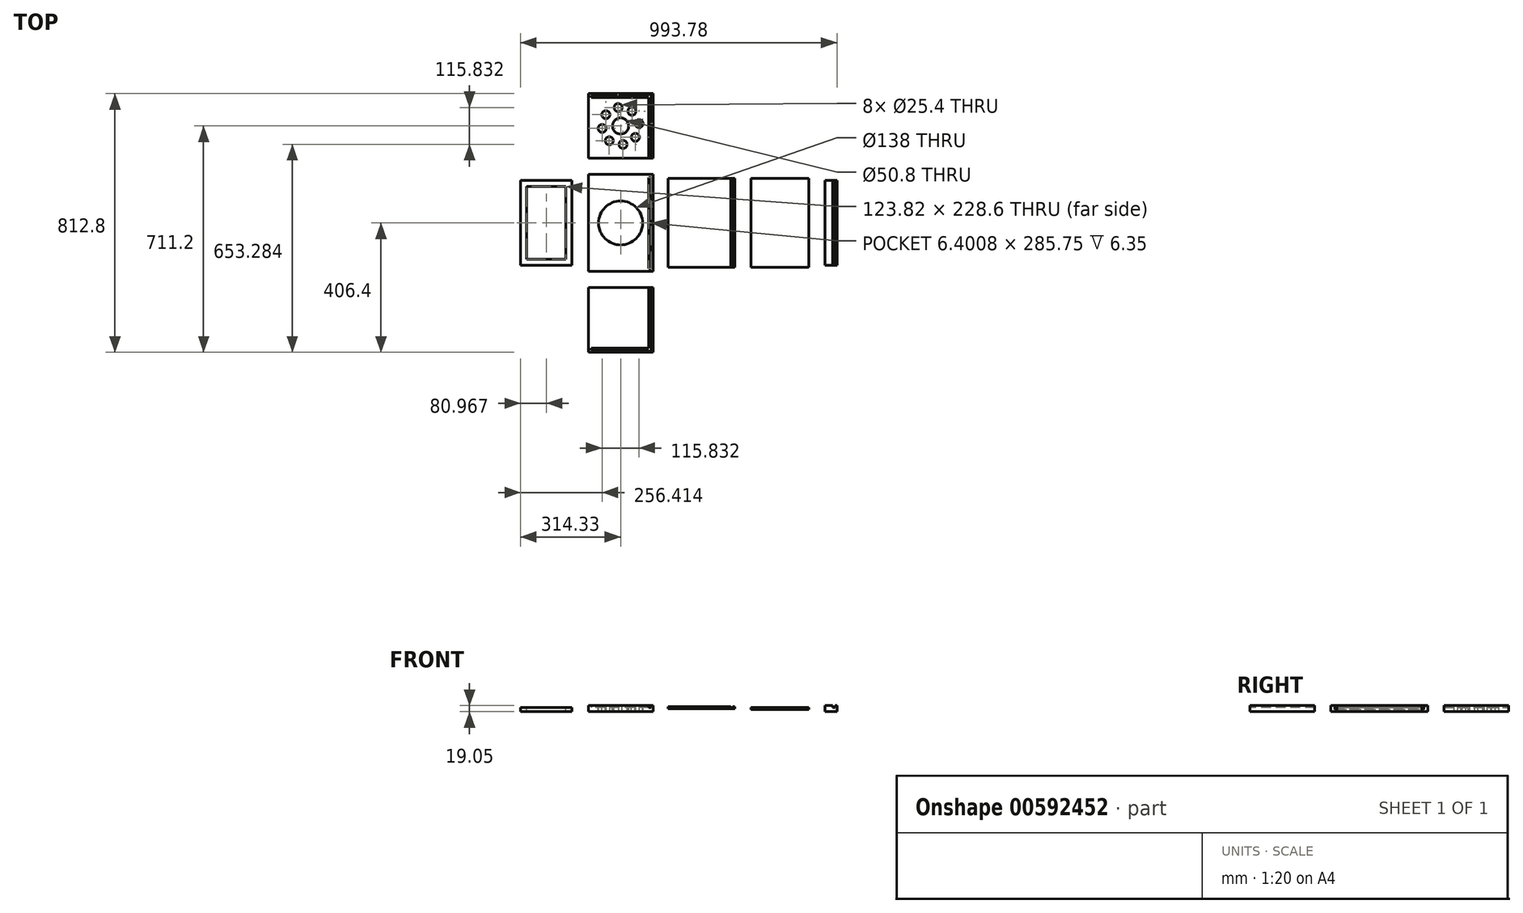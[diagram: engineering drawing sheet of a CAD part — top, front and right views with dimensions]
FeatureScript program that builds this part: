
annotation { "Feature Type Name" : "Feature", "Feature Type Description" : "" }
export const myFeature = defineFeature(function(context is Context, id is Id, definition is map)
    precondition{}
    {
        {
            var Q0;
            Q0=qCreatedBy(makeId("Top.planeOp"),FACE);
            var sketch = newSketch(context, id + "F0", { "sketchPlane" : qUnion([Q0])});
            skLineSegment(sketch, "E0.bottom", {"start": v(101.6, -152.4) * mm, "end": v(-101.6, -152.4) * mm});
            skLineSegment(sketch, "E0.top", {"start": v(101.6, 152.4) * mm, "end": v(-101.6, 152.4) * mm});
            skLineSegment(sketch, "E0.left", {"start": v(101.6, -152.4) * mm, "end": v(101.6, 152.4) * mm});
            skLineSegment(sketch, "E0.right", {"start": v(-101.6, -152.4) * mm, "end": v(-101.6, 152.4) * mm});
            skPoint(sketch, "E0.middle", {"position": v(0, 0) * mm});
            skCircle(sketch, "E1", {"center": v(0, 0) * mm, "radius": 69 * mm});
            skLineSegment(sketch, "E2.bottom", {"start": v(88.85, 142.88) * mm, "end": v(95.25, 142.88) * mm});
            skLineSegment(sketch, "E2.top", {"start": v(88.85, -142.88) * mm, "end": v(95.25, -142.88) * mm});
            skLineSegment(sketch, "E2.left", {"start": v(88.85, 142.88) * mm, "end": v(88.85, -142.88) * mm});
            skLineSegment(sketch, "E2.right", {"start": v(95.25, 142.88) * mm, "end": v(95.25, -142.88) * mm});
            skSolve(sketch);
        }
        {
            var Q0;
            Q0=makeQuery(id+"F0.imprint","IMPRINT",FACE,{"disambiguationData":[TD([[makeQuery(id+"F0.imprint","IMPRINT",EDGE,{"derivedFrom":sQuery(id+"F0.wireOp",EDGE,"E0.bottom")}),-1.0]])]});
            var Q1;
            {var subQ0=sQuery(id+"F0.wireOp",EDGE,"E0.right");Q1=makeQuery(id+"F0.imprint","IMPRINT",FACE,{"disambiguationData":[TD([[makeQuery(id+"F0.imprint","IMPRINT",EDGE,{"derivedFrom":subQ0}),-1.0]])]});}
            var Q2;
            Q2=makeQuery(id+"F0.imprint","IMPRINT",FACE,{"disambiguationData":[TD([[makeQuery(id+"F0.imprint","IMPRINT",EDGE,{"derivedFrom":sQuery(id+"F0.wireOp",EDGE,"E2.bottom")}),-1.0]])]});
            extrude(context, id + "F1", {"entities" : qUnion([Q0, Q1, Q2]), "oppositeDirection" : true, "depth" : 12.7 * mm, "offsetDistance" : 25.4 * mm});
        }
        {
            var Q0;
            {var subQ0=sQuery(id+"F0.wireOp",EDGE,"E0.right");Q0=makeQuery(id+"F0.imprint","IMPRINT",FACE,{"disambiguationData":[TD([[makeQuery(id+"F0.imprint","IMPRINT",EDGE,{"derivedFrom":subQ0}),-1.0]])]});}
            var Q1;
            {var subQ0=sQuery(id+"F0.wireOp",EDGE,"E0.left");Q1=makeQuery(id+"F0.imprint","IMPRINT",FACE,{"disambiguationData":[TD([[makeQuery(id+"F0.imprint","IMPRINT",EDGE,{"derivedFrom":subQ0}),1.0]])]});}
            extrude(context, id + "F2", {"entities" : qUnion([Q0, Q1]), "operationType" : NewBodyOperationType.ADD, "depth" : 6.35 * mm, "offsetDistance" : 25.4 * mm});
        }
        {
            var Q0;
            Q0=qCreatedBy(makeId("Top.planeOp"),FACE);
            var sketch = newSketch(context, id + "F3", { "sketchPlane" : qUnion([Q0])});
            skLineSegment(sketch, "E3.bottom", {"start": v(101.6, -406.4) * mm, "end": v(-101.6, -406.4) * mm});
            skLineSegment(sketch, "E3.top", {"start": v(101.6, -203.2) * mm, "end": v(-101.6, -203.2) * mm});
            skLineSegment(sketch, "E3.left", {"start": v(101.6, -406.4) * mm, "end": v(101.6, -203.2) * mm});
            skLineSegment(sketch, "E3.right", {"start": v(-101.6, -406.4) * mm, "end": v(-101.6, -203.2) * mm});
            skPoint(sketch, "E3.middle", {"position": v(0, -304.8) * mm});
            skPoint(sketch, "E4.0", {"position": v(101.6, -152.4) * mm});
            skPoint(sketch, "E4.1", {"position": v(-101.6, -152.4) * mm});
            skPoint(sketch, "E5.0", {"position": v(88.85, -142.88) * mm});
            skPoint(sketch, "E5.1", {"position": v(95.25, -142.88) * mm});
            skLineSegment(sketch, "E6.bottom", {"start": v(88.85, -200.03) * mm, "end": v(95.25, -200.03) * mm});
            skLineSegment(sketch, "E6.top", {"start": v(88.85, -409.58) * mm, "end": v(95.25, -409.58) * mm});
            skLineSegment(sketch, "E6.left", {"start": v(88.85, -200.03) * mm, "end": v(88.85, -409.58) * mm});
            skLineSegment(sketch, "E6.right", {"start": v(95.25, -200.03) * mm, "end": v(95.25, -409.58) * mm});
            skLineSegment(sketch, "E7.bottom", {"start": v(91.54, -393.65) * mm, "end": v(-92.07, -393.65) * mm});
            skLineSegment(sketch, "E7.top", {"start": v(91.54, -400.05) * mm, "end": v(-92.07, -400.05) * mm});
            skLineSegment(sketch, "E7.left", {"start": v(91.54, -393.65) * mm, "end": v(91.54, -400.05) * mm});
            skLineSegment(sketch, "E7.right", {"start": v(-92.07, -393.65) * mm, "end": v(-92.07, -400.05) * mm});
            skSolve(sketch);
        }
        {
            var Q0;
            Q0=makeQuery(id+"F3.imprint","IMPRINT",FACE,{"disambiguationData":[TD([[makeQuery(id+"F3.imprint","IMPRINT",EDGE,{"derivedFrom":sQuery(id+"F3.wireOp",EDGE,"E3.bottom")}),-1.0]])]});
            var Q1;
            {var subQ5=sQuery(id+"F3.wireOp",EDGE,"E3.right");Q1=makeQuery(id+"F3.imprint","IMPRINT",FACE,{"disambiguationData":[TD([[makeQuery(id+"F3.imprint","IMPRINT",EDGE,{"derivedFrom":subQ5}),-1.0]])]});}
            var Q2;
            {var subQ11=sQuery(id+"F3.wireOp",EDGE,"E7.left");Q2=makeQuery(id+"F3.imprint","IMPRINT",FACE,{"disambiguationData":[TD([[makeQuery(id+"F3.imprint","IMPRINT",EDGE,{"derivedFrom":subQ11}),1.0]])]});}
            var Q3;
            {var subQ5=sQuery(id+"F3.wireOp",EDGE,"E7.right");Q3=makeQuery(id+"F3.imprint","IMPRINT",FACE,{"disambiguationData":[TD([[makeQuery(id+"F3.imprint","IMPRINT",EDGE,{"derivedFrom":subQ5}),1.0]])]});}
            var Q4;
            {var subQ5=sQuery(id+"F3.wireOp",EDGE,"E7.left");Q4=makeQuery(id+"F3.imprint","IMPRINT",FACE,{"disambiguationData":[TD([[makeQuery(id+"F3.imprint","IMPRINT",EDGE,{"derivedFrom":subQ5}),-1.0]])]});}
            extrude(context, id + "F4", {"entities" : qUnion([Q0, Q1, Q2, Q3, Q4]), "oppositeDirection" : true, "depth" : 12.7 * mm, "offsetDistance" : 25.4 * mm});
        }
        {
            var Q0;
            {var subQ0=sQuery(id+"F3.wireOp",EDGE,"E3.right");Q0=makeQuery(id+"F3.imprint","IMPRINT",FACE,{"disambiguationData":[TD([[makeQuery(id+"F3.imprint","IMPRINT",EDGE,{"derivedFrom":subQ0}),-1.0]])]});}
            var Q1;
            {var subQ0=sQuery(id+"F3.wireOp",EDGE,"E3.left");Q1=makeQuery(id+"F3.imprint","IMPRINT",FACE,{"disambiguationData":[TD([[makeQuery(id+"F3.imprint","IMPRINT",EDGE,{"derivedFrom":subQ0}),1.0]])]});}
            extrude(context, id + "F5", {"entities" : qUnion([Q0, Q1]), "operationType" : NewBodyOperationType.ADD, "depth" : 6.35 * mm, "offsetDistance" : 25.4 * mm});
        }
        {
            var Q0;
            Q0=qCreatedBy(makeId("Top.planeOp"),FACE);
            var sketch = newSketch(context, id + "F6", { "sketchPlane" : qUnion([Q0])});
            skLineSegment(sketch, "E8.bottom", {"start": v(101.6, 203.2) * mm, "end": v(-101.6, 203.2) * mm});
            skLineSegment(sketch, "E8.top", {"start": v(101.6, 406.4) * mm, "end": v(-101.6, 406.4) * mm});
            skLineSegment(sketch, "E8.left", {"start": v(101.6, 203.2) * mm, "end": v(101.6, 406.4) * mm});
            skLineSegment(sketch, "E8.right", {"start": v(-101.6, 203.2) * mm, "end": v(-101.6, 406.4) * mm});
            skPoint(sketch, "E9.0", {"position": v(88.85, 142.88) * mm});
            skPoint(sketch, "E9.1", {"position": v(95.25, 142.88) * mm});
            skLineSegment(sketch, "E10.bottom", {"start": v(88.85, 200.03) * mm, "end": v(95.25, 200.03) * mm});
            skLineSegment(sketch, "E10.top", {"start": v(88.85, 409.58) * mm, "end": v(95.25, 409.58) * mm});
            skLineSegment(sketch, "E10.left", {"start": v(88.85, 200.03) * mm, "end": v(88.85, 409.58) * mm});
            skLineSegment(sketch, "E10.right", {"start": v(95.25, 200.03) * mm, "end": v(95.25, 409.58) * mm});
            skLineSegment(sketch, "E11.bottom", {"start": v(91.88, 400.05) * mm, "end": v(-92.08, 400.05) * mm});
            skLineSegment(sketch, "E11.top", {"start": v(91.88, 393.65) * mm, "end": v(-92.08, 393.65) * mm});
            skLineSegment(sketch, "E11.left", {"start": v(91.88, 400.05) * mm, "end": v(91.88, 393.65) * mm});
            skLineSegment(sketch, "E11.right", {"start": v(-92.08, 400.05) * mm, "end": v(-92.08, 393.65) * mm});
            skCircle(sketch, "E12", {"center": v(-46.37, 340.34) * mm, "radius": 12.7 * mm});
            skCircle(sketch, "E13.1.0", {"center": v(-57.92, 297.14) * mm, "radius": 12.7 * mm});
            skCircle(sketch, "E13.2.0", {"center": v(-35.54, 258.43) * mm, "radius": 12.7 * mm});
            skCircle(sketch, "E13.3.0", {"center": v(7.66, 246.88) * mm, "radius": 12.7 * mm});
            skCircle(sketch, "E13.4.0", {"center": v(46.37, 269.26) * mm, "radius": 12.7 * mm});
            skCircle(sketch, "E13.5.0", {"center": v(57.92, 312.46) * mm, "radius": 12.7 * mm});
            skCircle(sketch, "E13.6.0", {"center": v(35.54, 351.17) * mm, "radius": 12.7 * mm});
            skCircle(sketch, "E13.7.0", {"center": v(-7.66, 362.72) * mm, "radius": 12.7 * mm});
            skPoint(sketch, "E13.center", {"position": v(0, 304.8) * mm});
            skCircle(sketch, "E14", {"center": v(0, 304.8) * mm, "radius": 25.4 * mm});
            skSolve(sketch);
        }
        {
            var Q0;
            Q0=makeQuery(id+"F6.imprint","IMPRINT",FACE,{"disambiguationData":[TD([[makeQuery(id+"F6.imprint","IMPRINT",EDGE,{"derivedFrom":sQuery(id+"F6.wireOp",EDGE,"E8.bottom")}),-1.0]])]});
            var Q1;
            {var subQ5=sQuery(id+"F6.wireOp",EDGE,"E11.right");Q1=makeQuery(id+"F6.imprint","IMPRINT",FACE,{"disambiguationData":[TD([[makeQuery(id+"F6.imprint","IMPRINT",EDGE,{"derivedFrom":subQ5}),1.0]])]});}
            var Q2;
            {var subQ5=sQuery(id+"F6.wireOp",EDGE,"E8.right");Q2=makeQuery(id+"F6.imprint","IMPRINT",FACE,{"disambiguationData":[TD([[makeQuery(id+"F6.imprint","IMPRINT",EDGE,{"derivedFrom":subQ5}),-1.0]])]});}
            var Q3;
            {var subQ11=sQuery(id+"F6.wireOp",EDGE,"E11.left");Q3=makeQuery(id+"F6.imprint","IMPRINT",FACE,{"disambiguationData":[TD([[makeQuery(id+"F6.imprint","IMPRINT",EDGE,{"derivedFrom":subQ11}),1.0]])]});}
            var Q4;
            {var subQ5=sQuery(id+"F6.wireOp",EDGE,"E11.left");Q4=makeQuery(id+"F6.imprint","IMPRINT",FACE,{"disambiguationData":[TD([[makeQuery(id+"F6.imprint","IMPRINT",EDGE,{"derivedFrom":subQ5}),-1.0]])]});}
            extrude(context, id + "F7", {"entities" : qUnion([Q0, Q1, Q2, Q3, Q4]), "oppositeDirection" : true, "depth" : 12.7 * mm, "offsetDistance" : 25.4 * mm});
        }
        {
            var Q0;
            {var subQ0=sQuery(id+"F6.wireOp",EDGE,"E8.right");Q0=makeQuery(id+"F6.imprint","IMPRINT",FACE,{"disambiguationData":[TD([[makeQuery(id+"F6.imprint","IMPRINT",EDGE,{"derivedFrom":subQ0}),-1.0]])]});}
            var Q1;
            {var subQ0=sQuery(id+"F6.wireOp",EDGE,"E8.left");Q1=makeQuery(id+"F6.imprint","IMPRINT",FACE,{"disambiguationData":[TD([[makeQuery(id+"F6.imprint","IMPRINT",EDGE,{"derivedFrom":subQ0}),1.0]])]});}
            extrude(context, id + "F8", {"entities" : qUnion([Q0, Q1]), "operationType" : NewBodyOperationType.ADD, "depth" : 6.35 * mm, "offsetDistance" : 25.4 * mm});
        }
        {
            var Q0;
            Q0=qCreatedBy(makeId("Top.planeOp"),FACE);
            var sketch = newSketch(context, id + "F9", { "sketchPlane" : qUnion([Q0])});
            skLineSegment(sketch, "E15.bottom", {"start": v(358.8, -139.7) * mm, "end": v(149.25, -139.7) * mm});
            skLineSegment(sketch, "E15.top", {"start": v(358.8, 139.7) * mm, "end": v(149.25, 139.7) * mm});
            skLineSegment(sketch, "E15.left", {"start": v(358.8, -139.7) * mm, "end": v(358.8, 139.7) * mm});
            skLineSegment(sketch, "E15.right", {"start": v(149.25, -139.7) * mm, "end": v(149.25, 139.7) * mm});
            skPoint(sketch, "E15.middle", {"position": v(254.02, 0) * mm});
            skLineSegment(sketch, "E16.bottom", {"start": v(346.05, 142.88) * mm, "end": v(352.45, 142.88) * mm});
            skLineSegment(sketch, "E16.top", {"start": v(346.05, -142.88) * mm, "end": v(352.45, -142.88) * mm});
            skLineSegment(sketch, "E16.left", {"start": v(346.05, 142.88) * mm, "end": v(346.05, -142.88) * mm});
            skLineSegment(sketch, "E16.right", {"start": v(352.45, 142.88) * mm, "end": v(352.45, -142.88) * mm});
            skSolve(sketch);
        }
        {
            var Q0;
            {var subQ0=sQuery(id+"F9.wireOp",EDGE,"E15.left");Q0=makeQuery(id+"F9.imprint","IMPRINT",FACE,{"disambiguationData":[TD([[makeQuery(id+"F9.imprint","IMPRINT",EDGE,{"derivedFrom":subQ0}),1.0]])]});}
            var Q1;
            {var subQ0=sQuery(id+"F9.wireOp",EDGE,"E16.right");var subQ1=sQuery(id+"F9.wireOp",EDGE,"E15.bottom");var subQ2=makeQuery(id+"F9.imprint","INTERSECT",VERTEX,{"derivedFrom":[subQ1,subQ0]});Q1=makeQuery(id+"F9.imprint","IMPRINT",FACE,{"disambiguationData":[TD([[makeQuery(id+"F9.imprint","IMPRINT",EDGE,{"disambiguationData":[TD([[subQ2,-1.0]])],"derivedFrom":subQ1}),-1.0]])]});}
            var Q2;
            {var subQ0=sQuery(id+"F9.wireOp",EDGE,"E15.right");Q2=makeQuery(id+"F9.imprint","IMPRINT",FACE,{"disambiguationData":[TD([[makeQuery(id+"F9.imprint","IMPRINT",EDGE,{"derivedFrom":subQ0}),-1.0]])]});}
            extrude(context, id + "F10", {"entities" : qUnion([Q0, Q1, Q2]), "oppositeDirection" : true, "depth" : 3.2 * mm, "offsetDistance" : 25.4 * mm});
        }
        {
            var Q0;
            Q0=qCreatedBy(makeId("Top.planeOp"),FACE);
            var sketch = newSketch(context, id + "F11", { "sketchPlane" : qUnion([Q0])});
            skLineSegment(sketch, "E17.bottom", {"start": v(-152.4, -133.35) * mm, "end": v(-314.33, -133.35) * mm});
            skLineSegment(sketch, "E17.top", {"start": v(-152.4, 133.35) * mm, "end": v(-314.33, 133.35) * mm});
            skLineSegment(sketch, "E17.left", {"start": v(-152.4, -133.35) * mm, "end": v(-152.4, 133.35) * mm});
            skLineSegment(sketch, "E17.right", {"start": v(-314.33, -133.35) * mm, "end": v(-314.33, 133.35) * mm});
            skPoint(sketch, "E17.middle", {"position": v(-233.36, 0) * mm});
            skLineSegment(sketch, "E18.bottom", {"start": v(-171.45, -114.3) * mm, "end": v(-295.28, -114.3) * mm});
            skLineSegment(sketch, "E18.top", {"start": v(-171.45, 114.3) * mm, "end": v(-295.28, 114.3) * mm});
            skLineSegment(sketch, "E18.left", {"start": v(-171.45, -114.3) * mm, "end": v(-171.45, 114.3) * mm});
            skLineSegment(sketch, "E18.right", {"start": v(-295.28, -114.3) * mm, "end": v(-295.28, 114.3) * mm});
            skSolve(sketch);
        }
        {
            var Q0;
            Q0=makeQuery(id+"F11.imprint","IMPRINT",FACE,{"disambiguationData":[TD([[makeQuery(id+"F11.imprint","IMPRINT",EDGE,{"derivedFrom":sQuery(id+"F11.wireOp",EDGE,"E17.bottom")}),-1.0]])]});
            extrude(context, id + "F12", {"entities" : qUnion([Q0]), "oppositeDirection" : true, "depth" : 12.7 * mm, "offsetDistance" : 25.4 * mm});
        }
        {
            var Q0;
            {var subQ0=sQuery(id+"F9.wireOp",EDGE,"E15.right");Q0=makeQuery(id+"F9.imprint","IMPRINT",FACE,{"disambiguationData":[TD([[makeQuery(id+"F9.imprint","IMPRINT",EDGE,{"derivedFrom":subQ0}),-1.0]])]});}
            var Q1;
            {var subQ0=sQuery(id+"F9.wireOp",EDGE,"E15.left");Q1=makeQuery(id+"F9.imprint","IMPRINT",FACE,{"disambiguationData":[TD([[makeQuery(id+"F9.imprint","IMPRINT",EDGE,{"derivedFrom":subQ0}),1.0]])]});}
            extrude(context, id + "F13", {"entities" : qUnion([Q0, Q1]), "operationType" : NewBodyOperationType.ADD, "depth" : 3.2 * mm, "offsetDistance" : 25.4 * mm});
        }
        {
            var Q0;
            Q0=qCreatedBy(makeId("Top.planeOp"),FACE);
            var sketch = newSketch(context, id + "F14", { "sketchPlane" : qUnion([Q0])});
            skPoint(sketch, "E19.0", {"position": v(358.8, -139.7) * mm});
            skPoint(sketch, "E19.1", {"position": v(358.8, 139.7) * mm});
            skLineSegment(sketch, "E20.bottom", {"start": v(409.6, -139.7) * mm, "end": v(590.55, -139.7) * mm});
            skLineSegment(sketch, "E20.top", {"start": v(409.6, 139.7) * mm, "end": v(590.55, 139.7) * mm});
            skLineSegment(sketch, "E20.left", {"start": v(409.6, -139.7) * mm, "end": v(409.6, 139.7) * mm});
            skLineSegment(sketch, "E20.right", {"start": v(590.55, -139.7) * mm, "end": v(590.55, 139.7) * mm});
            skSolve(sketch);
        }
        {
            var Q0;
            Q0=makeQuery(id+"F14.imprint","IMPRINT",FACE,{"disambiguationData":[TD([[makeQuery(id+"F14.imprint","IMPRINT",EDGE,{"derivedFrom":sQuery(id+"F14.wireOp",EDGE,"E20.bottom")}),1.0]])]});
            extrude(context, id + "F15", {"entities" : qUnion([Q0]), "oppositeDirection" : true, "depth" : 6.4 * mm, "offsetDistance" : 25.4 * mm});
        }
        {
            var Q0;
            Q0=makeQuery(id+"F0.imprint","IMPRINT",FACE,{"disambiguationData":[TD([[makeQuery(id+"F0.imprint","IMPRINT",EDGE,{"derivedFrom":sQuery(id+"F0.wireOp",EDGE,"E1")}),1.0]])]});
            var sketch = newSketch(context, id + "F16", { "sketchPlane" : qUnion([Q0])});
            skPoint(sketch, "E21.0", {"position": v(101.6, 133.35) * mm});
            skPoint(sketch, "E21.1", {"position": v(101.6, -133.35) * mm});
            skLineSegment(sketch, "E22.bottom", {"start": v(641.35, 133.35) * mm, "end": v(679.45, 133.35) * mm});
            skLineSegment(sketch, "E22.top", {"start": v(641.35, -133.35) * mm, "end": v(679.45, -133.35) * mm});
            skLineSegment(sketch, "E22.left", {"start": v(641.35, 133.35) * mm, "end": v(641.35, -133.35) * mm});
            skLineSegment(sketch, "E22.right", {"start": v(679.45, 133.35) * mm, "end": v(679.45, -133.35) * mm});
            skLineSegment(sketch, "E23.bottom", {"start": v(666.7, 136.53) * mm, "end": v(673.1, 136.53) * mm});
            skLineSegment(sketch, "E23.top", {"start": v(666.7, -136.53) * mm, "end": v(673.1, -136.53) * mm});
            skLineSegment(sketch, "E23.left", {"start": v(666.7, 136.53) * mm, "end": v(666.7, -136.53) * mm});
            skLineSegment(sketch, "E23.right", {"start": v(673.1, 136.53) * mm, "end": v(673.1, -136.53) * mm});
            skSolve(sketch);
        }
        {
            var Q0;
            {var subQ0=sQuery(id+"F16.wireOp",EDGE,"E22.left");Q0=makeQuery(id+"F16.imprint","IMPRINT",FACE,{"disambiguationData":[TD([[makeQuery(id+"F16.imprint","IMPRINT",EDGE,{"derivedFrom":subQ0}),1.0]])]});}
            var Q1;
            {var subQ0=sQuery(id+"F16.wireOp",EDGE,"E23.left");var subQ1=sQuery(id+"F16.wireOp",EDGE,"E22.bottom");var subQ2=makeQuery(id+"F16.imprint","INTERSECT",VERTEX,{"derivedFrom":[subQ1,subQ0]});Q1=makeQuery(id+"F16.imprint","IMPRINT",FACE,{"disambiguationData":[TD([[makeQuery(id+"F16.imprint","IMPRINT",EDGE,{"disambiguationData":[TD([[subQ2,-1.0]])],"derivedFrom":subQ1}),-1.0]])]});}
            var Q2;
            {var subQ0=sQuery(id+"F16.wireOp",EDGE,"E22.right");Q2=makeQuery(id+"F16.imprint","IMPRINT",FACE,{"disambiguationData":[TD([[makeQuery(id+"F16.imprint","IMPRINT",EDGE,{"derivedFrom":subQ0}),-1.0]])]});}
            extrude(context, id + "F17", {"entities" : qUnion([Q0, Q1, Q2]), "oppositeDirection" : true, "depth" : 12.7 * mm, "offsetDistance" : 25.4 * mm});
        }
        {
            var Q0;
            {var subQ0=sQuery(id+"F16.wireOp",EDGE,"E22.left");Q0=makeQuery(id+"F16.imprint","IMPRINT",FACE,{"disambiguationData":[TD([[makeQuery(id+"F16.imprint","IMPRINT",EDGE,{"derivedFrom":subQ0}),1.0]])]});}
            var Q1;
            {var subQ0=sQuery(id+"F16.wireOp",EDGE,"E22.right");Q1=makeQuery(id+"F16.imprint","IMPRINT",FACE,{"disambiguationData":[TD([[makeQuery(id+"F16.imprint","IMPRINT",EDGE,{"derivedFrom":subQ0}),-1.0]])]});}
            extrude(context, id + "F18", {"entities" : qUnion([Q0, Q1]), "operationType" : NewBodyOperationType.ADD, "depth" : 6.35 * mm, "offsetDistance" : 25.4 * mm});
        }
    });
